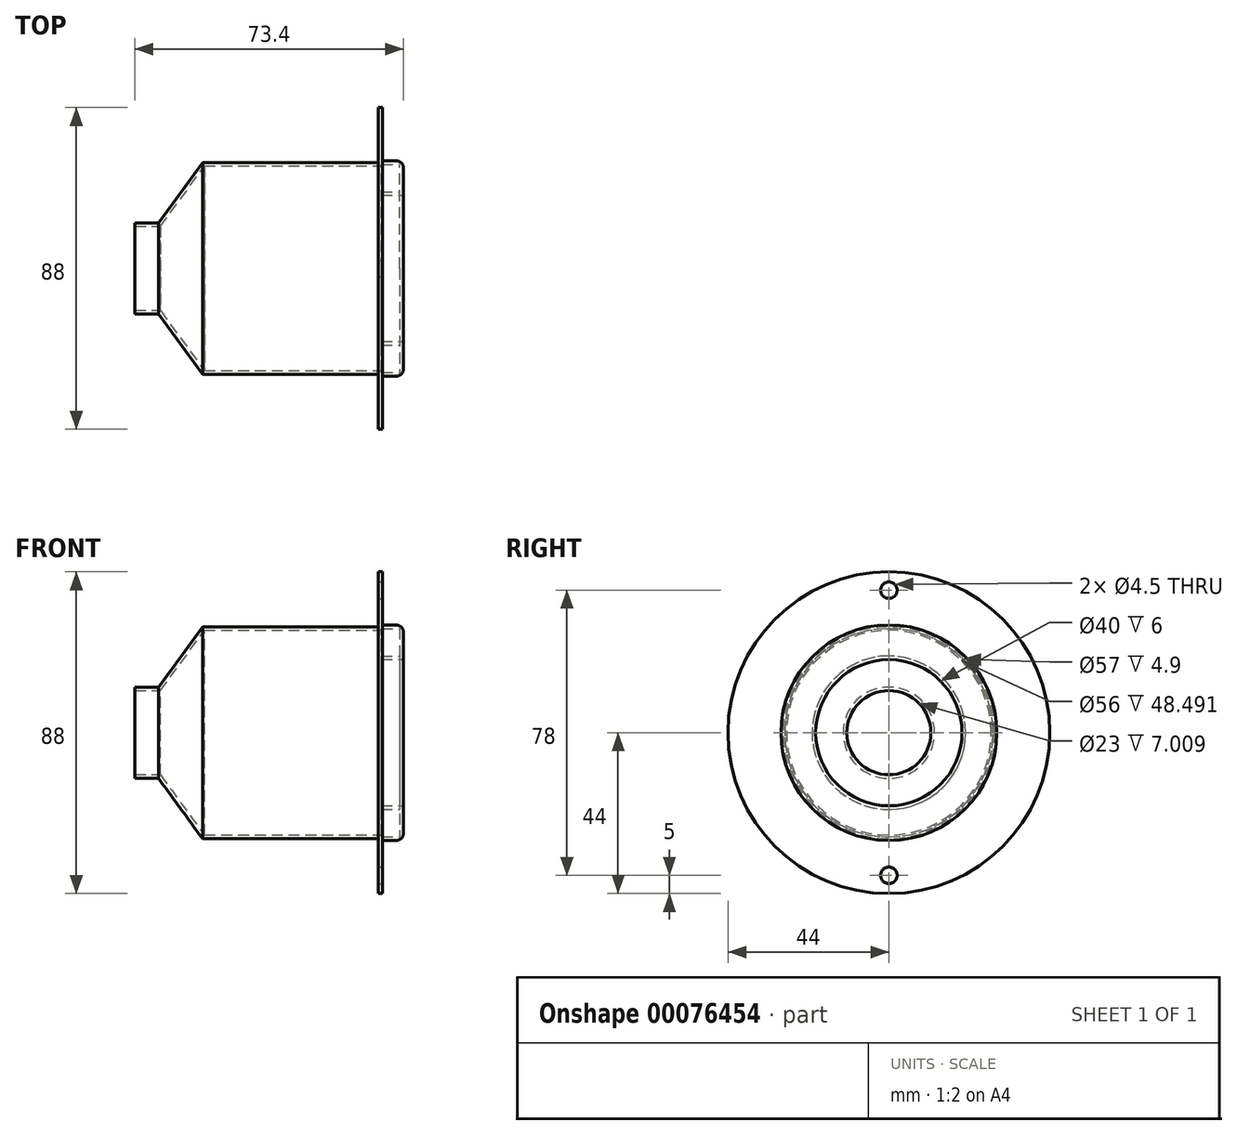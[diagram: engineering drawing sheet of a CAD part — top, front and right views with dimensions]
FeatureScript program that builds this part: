
annotation { "Feature Type Name" : "Feature", "Feature Type Description" : "" }
export const myFeature = defineFeature(function(context is Context, id is Id, definition is map)
    precondition{}
    {
        {
            var Q0;
            Q0=qCreatedBy(makeId("Front.planeOp"),FACE);
            var sketch = newSketch(context, id + "F0", { "sketchPlane" : qUnion([Q0])});
            skLineSegment(sketch, "E0", {"start": v(0, 0) * mm, "end": v(0, 12.5) * mm});
            skLineSegment(sketch, "E1", {"start": v(0, 12.5) * mm, "end": v(6.5, 12.5) * mm});
            skLineSegment(sketch, "E2", {"start": v(6.5, 12.5) * mm, "end": v(18.5, 29) * mm});
            skLineSegment(sketch, "E3", {"start": v(18.5, 29) * mm, "end": v(66.5, 29) * mm});
            skLineSegment(sketch, "E4", {"start": v(66.5, 29) * mm, "end": v(66.5, 44) * mm});
            skLineSegment(sketch, "E5", {"start": v(66.5, 44) * mm, "end": v(67.7, 44) * mm});
            skLineSegment(sketch, "E6", {"start": v(67.7, 44) * mm, "end": v(67.7, 29.5) * mm});
            skLineSegment(sketch, "E7", {"start": v(67.7, 29.5) * mm, "end": v(73.4, 29.5) * mm});
            skLineSegment(sketch, "E8", {"start": v(73.4, 29.5) * mm, "end": v(73.4, 0) * mm});
            skLineSegment(sketch, "E9", {"start": v(73.4, 0) * mm, "end": v(0, 0) * mm});
            skSolve(sketch);
        }
        {
            var Q0;
            Q0=makeQuery(id+"F0.imprint","IMPRINT",FACE,{"disambiguationData":[TD([[makeQuery(id+"F0.imprint","IMPRINT",EDGE,{"derivedFrom":sQuery(id+"F0.wireOp",EDGE,"E0")}),-1.0]])]});
            var Q1;
            Q1=sQuery(id+"F0.wireOp",EDGE,"E9");
            revolve(context, id + "F1", {"entities" : qUnion([Q0]), "axis" : qUnion([Q1]), "revolveType" : RevolveType.FULL});
        }
        {
            var Q0;
            Q0=makeQuery(id+"F1.opRevolve","SWEPT_FACE",FACE,{"disambiguationData":[OSD([sQuery(id+"F0.wireOp",EDGE,"E8")])]});
            var sketch = newSketch(context, id + "F2", { "sketchPlane" : qUnion([Q0])});
            skCircle(sketch, "E10", {"center": v(0, 0) * mm, "radius": 20 * mm});
            skSolve(sketch);
        }
        {
            var Q0;
            Q0=makeQuery(id+"F2.imprint","IMPRINT",FACE,{"disambiguationData":[TD([[makeQuery(id+"F2.imprint","IMPRINT",EDGE,{"derivedFrom":sQuery(id+"F2.wireOp",EDGE,"E10")}),1.0]])]});
            extrude(context, id + "F3", {"entities" : qUnion([Q0]), "operationType" : NewBodyOperationType.REMOVE, "oppositeDirection" : true, "depth" : 6 * mm});
        }
        {
            var Q0;
            Q0=makeQuery(id+"F3.boolean.opBoolean","COPY",FACE,{"derivedFrom":makeQuery(id+"F3.opExtrude","CAP_FACE",FACE,{"disambiguationData":[OSD([sQuery(id+"F2.wireOp",EDGE,"E10")])],"isStart":false})});
            var Q1;
            Q1=makeQuery(id+"F1.opRevolve","SWEPT_FACE",FACE,{"disambiguationData":[OSD([sQuery(id+"F0.wireOp",EDGE,"E0")])]});
            var Q2;
            Q2=makeQuery(id+"F1.opRevolve","SWEPT_BODY",BODY,{"disambiguationData":[OSD([sQuery(id+"F0.wireOp",EDGE,"E0"),sQuery(id+"F0.wireOp",EDGE,"E1"),sQuery(id+"F0.wireOp",EDGE,"E2"),sQuery(id+"F0.wireOp",EDGE,"E3"),sQuery(id+"F0.wireOp",EDGE,"E4"),sQuery(id+"F0.wireOp",EDGE,"E5"),sQuery(id+"F0.wireOp",EDGE,"E6"),sQuery(id+"F0.wireOp",EDGE,"E7"),sQuery(id+"F0.wireOp",EDGE,"E8"),sQuery(id+"F0.wireOp",EDGE,"E9")])]});
            shell(context, id + "F4", {"entities" : qUnion([Q0, Q1]), "parts" : qUnion([Q2]), "thickness" : 1 * mm});
        }
        {
            var Q0;
            Q0=makeQuery(id+"F1.opRevolve","SWEPT_EDGE",EDGE,{"disambiguationData":[OSD([sQuery(id+"F0.wireOp",EDGE,"E7"),sQuery(id+"F0.wireOp",EDGE,"E8")])]});
            var Q1;
            Q1=makeQuery(id+"F3.boolean.opBoolean","COPY",EDGE,{"derivedFrom":makeQuery(id+"F3.opExtrude","CAP_EDGE",EDGE,{"disambiguationData":[OSD([sQuery(id+"F2.wireOp",EDGE,"E10")])],"isStart":true})});
            fillet(context, id + "F5", {"entities" : qUnion([Q0, Q1]), "radius" : 2 * mm, "tangentPropagation" : true, "allowEdgeOverflow" : false});
        }
        {
            var Q0;
            Q0=makeQuery(id+"F1.opRevolve","SWEPT_FACE",FACE,{"disambiguationData":[OSD([sQuery(id+"F0.wireOp",EDGE,"E6")])]});
            var sketch = newSketch(context, id + "F6", { "sketchPlane" : qUnion([Q0])});
            skPoint(sketch, "E11", {"position": v(0, 39) * mm});
            skPoint(sketch, "E12", {"position": v(0, -39) * mm});
            skLineSegment(sketch, "E13", {"start": v(0, 0) * mm, "end": v(15.28, 0) * mm, "construction": true});
            skSolve(sketch);
        }
        {
            var Q0;
            Q0=sQuery(id+"F6.wireOp",VERTEX,"E11");
            var Q1;
            Q1=sQuery(id+"F6.wireOp",VERTEX,"E12");
            var Q2;
            Q2=makeQuery(id+"F1.opRevolve","SWEPT_BODY",BODY,{"disambiguationData":[OSD([sQuery(id+"F0.wireOp",EDGE,"E0"),sQuery(id+"F0.wireOp",EDGE,"E1"),sQuery(id+"F0.wireOp",EDGE,"E2"),sQuery(id+"F0.wireOp",EDGE,"E3"),sQuery(id+"F0.wireOp",EDGE,"E4"),sQuery(id+"F0.wireOp",EDGE,"E5"),sQuery(id+"F0.wireOp",EDGE,"E6"),sQuery(id+"F0.wireOp",EDGE,"E7"),sQuery(id+"F0.wireOp",EDGE,"E8"),sQuery(id+"F0.wireOp",EDGE,"E9")])]});
            hole(context, id + "F7", {"style" : HoleStyle.SIMPLE, "endStyle" : HoleEndStyle.THROUGH, "standardTappedOrClearance" : lookupTablePath({ "standard" : "ISO", "size" : "4.5", "type" : "Drilled" }), "standardBlindInLast" : lookupTablePath({ "standard" : "ISO", "size" : "4.5", "type" : "Drilled" }), "holeDiameter" : 4.5 * mm, "startFromSketch" : true, "locations" : qUnion([Q0, Q1]), "scope" : qUnion([Q2]), "isTappedThrough" : true});
        }
    });
